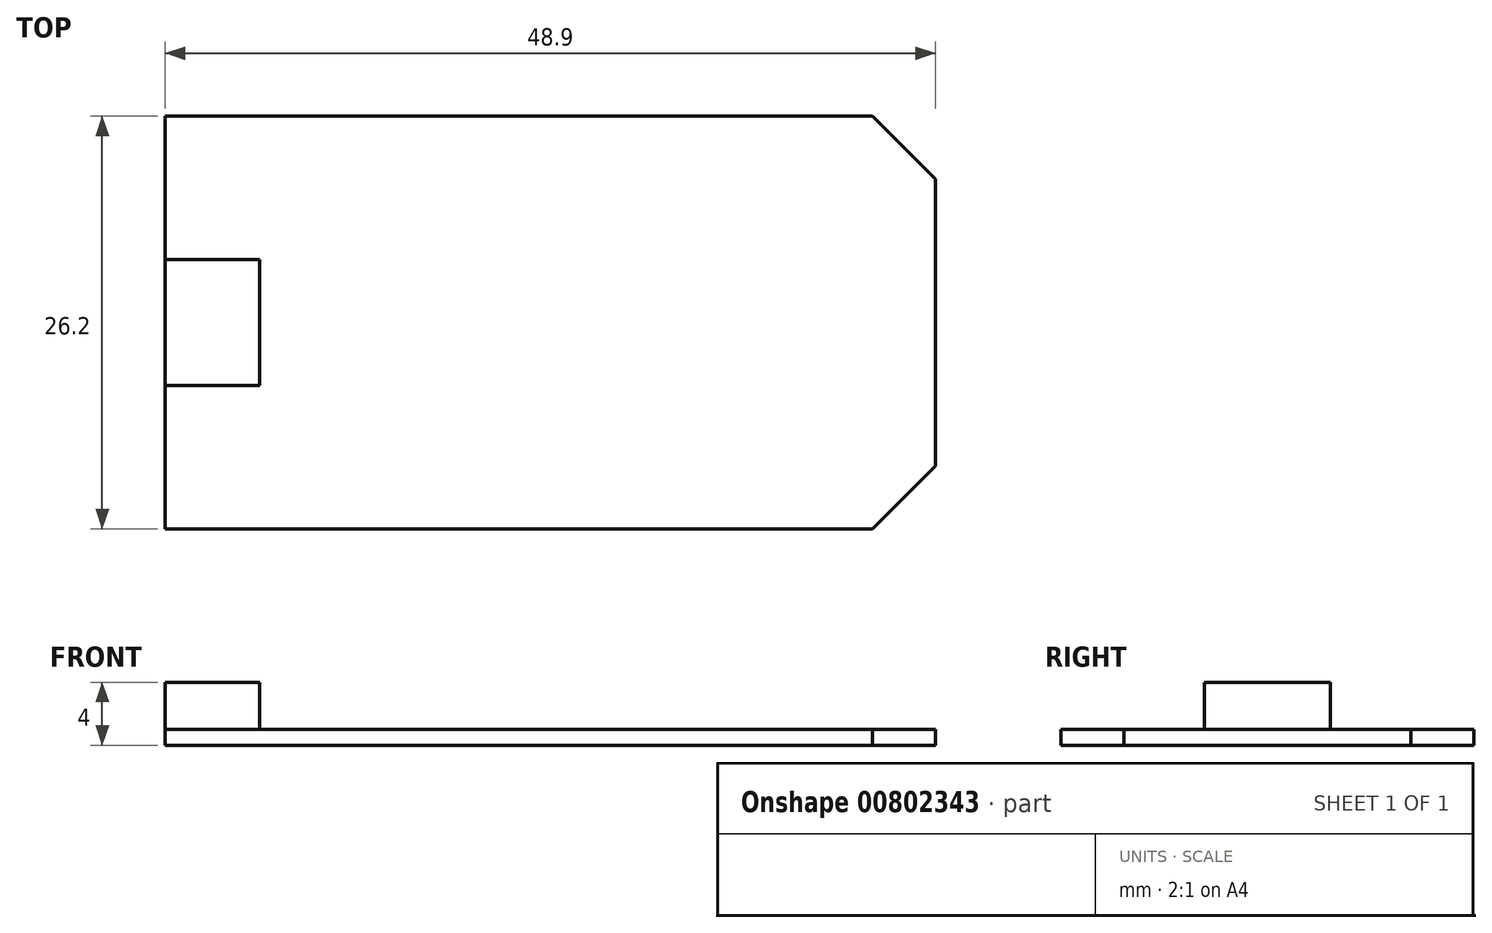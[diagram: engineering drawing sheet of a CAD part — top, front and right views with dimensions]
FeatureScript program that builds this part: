
annotation { "Feature Type Name" : "Feature", "Feature Type Description" : "" }
export const myFeature = defineFeature(function(context is Context, id is Id, definition is map)
    precondition{}
    {
        {
            var Q0;
            Q0=qCreatedBy(makeId("Top.planeOp"),FACE);
            var sketch = newSketch(context, id + "F0", { "sketchPlane" : qUnion([Q0])});
            skLineSegment(sketch, "E0.bottom", {"start": v(-24.45, -13.1) * mm, "end": v(24.45, -13.1) * mm});
            skLineSegment(sketch, "E0.top", {"start": v(-24.45, 13.1) * mm, "end": v(24.45, 13.1) * mm});
            skLineSegment(sketch, "E0.left", {"start": v(-24.45, -13.1) * mm, "end": v(-24.45, 13.1) * mm});
            skLineSegment(sketch, "E0.right", {"start": v(24.45, -13.1) * mm, "end": v(24.45, 13.1) * mm});
            skPoint(sketch, "E0.middle", {"position": v(0, 0) * mm});
            skSolve(sketch);
        }
        {
            var Q0;
            Q0 = qSketchRegion(id + "F0", true);
            extrude(context, id + "F1", {"entities" : qUnion([Q0]), "depth" : 1 * mm, "offsetDistance" : 25 * mm});
        }
        {
            var Q0;
            Q0=makeQuery(id+"F1.opExtrude","SWEPT_EDGE",EDGE,{"disambiguationData":[OSD([sQuery(id+"F0.wireOp",EDGE,"E0.top"),sQuery(id+"F0.wireOp",EDGE,"E0.right")])]});
            var Q1;
            Q1=makeQuery(id+"F1.opExtrude","SWEPT_EDGE",EDGE,{"disambiguationData":[OSD([sQuery(id+"F0.wireOp",EDGE,"E0.bottom"),sQuery(id+"F0.wireOp",EDGE,"E0.right")])]});
            chamfer(context, id + "F2", {"entities" : qUnion([Q0, Q1]), "width" : 4 * mm, "tangentPropagation" : true});
        }
        {
            var Q0;
            Q0=makeQuery(id+"F1.opExtrude","CAP_FACE",FACE,{"disambiguationData":[OSD([sQuery(id+"F0.wireOp",EDGE,"E0.bottom"),sQuery(id+"F0.wireOp",EDGE,"E0.top"),sQuery(id+"F0.wireOp",EDGE,"E0.left"),sQuery(id+"F0.wireOp",EDGE,"E0.right")])],"isStart":false});
            var sketch = newSketch(context, id + "F3", { "sketchPlane" : qUnion([Q0])});
            skLineSegment(sketch, "E1.bottom", {"start": v(-24.45, 4) * mm, "end": v(-18.45, 4) * mm});
            skLineSegment(sketch, "E1.top", {"start": v(-24.45, -4) * mm, "end": v(-18.45, -4) * mm});
            skLineSegment(sketch, "E1.left", {"start": v(-24.45, 4) * mm, "end": v(-24.45, -4) * mm});
            skLineSegment(sketch, "E1.right", {"start": v(-18.45, 4) * mm, "end": v(-18.45, -4) * mm});
            skSolve(sketch);
        }
        {
            var Q0;
            Q0 = qSketchRegion(id + "F3", true);
            extrude(context, id + "F4", {"entities" : qUnion([Q0]), "operationType" : NewBodyOperationType.ADD, "depth" : 3 * mm, "offsetDistance" : 25 * mm});
        }
    });
